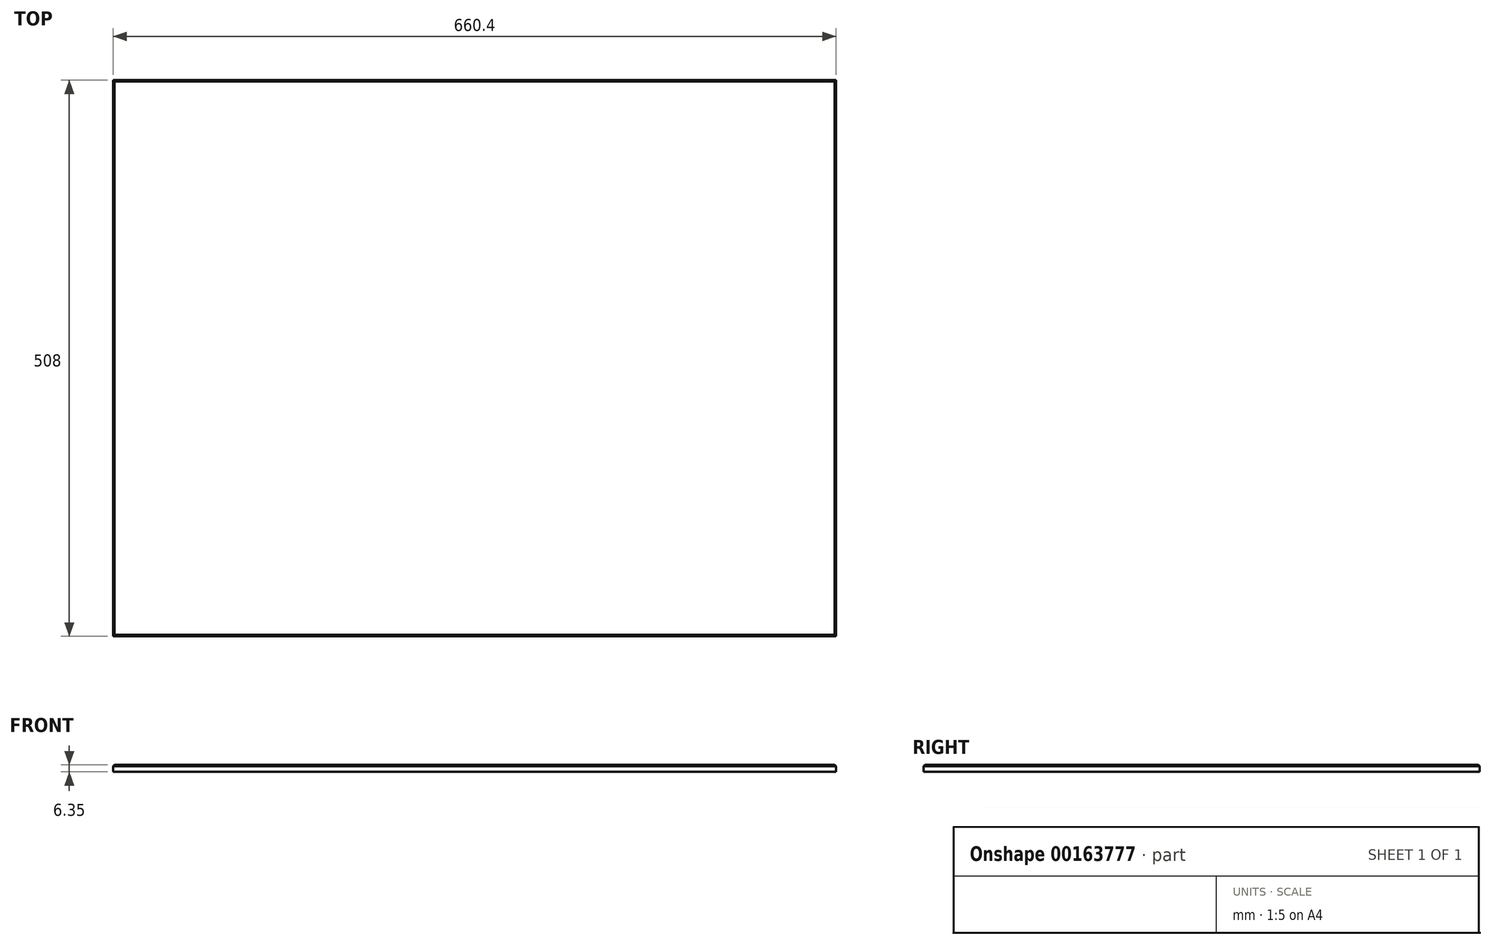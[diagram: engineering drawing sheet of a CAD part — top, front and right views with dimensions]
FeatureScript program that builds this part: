
annotation { "Feature Type Name" : "Feature", "Feature Type Description" : "" }
export const myFeature = defineFeature(function(context is Context, id is Id, definition is map)
    precondition{}
    {
        {
            var Q0;
            Q0=qCreatedBy(makeId("Top.planeOp"),FACE);
            var sketch = newSketch(context, id + "F0", { "sketchPlane" : qUnion([Q0])});
            skLineSegment(sketch, "E0.bottom", {"start": v(330.2, 254) * mm, "end": v(-330.2, 254) * mm});
            skLineSegment(sketch, "E0.top", {"start": v(330.2, -254) * mm, "end": v(-330.2, -254) * mm});
            skLineSegment(sketch, "E0.left", {"start": v(330.2, 254) * mm, "end": v(330.2, -254) * mm});
            skLineSegment(sketch, "E0.right", {"start": v(-330.2, 254) * mm, "end": v(-330.2, -254) * mm});
            skPoint(sketch, "E0.middle", {"position": v(0, 0) * mm});
            skSolve(sketch);
        }
        {
            var Q0;
            Q0=qSketchRegion(id+"F0",true);
            extrude(context, id + "F1", {"entities" : qUnion([Q0]), "depth" : 6.35 * mm});
        }
        {
            var Q0;
            Q0=makeQuery(id+"F1.opExtrude","CAP_FACE",FACE,{"disambiguationData":[OSD([sQuery(id+"F0.wireOp",EDGE,"E0.bottom"),sQuery(id+"F0.wireOp",EDGE,"E0.top"),sQuery(id+"F0.wireOp",EDGE,"E0.left"),sQuery(id+"F0.wireOp",EDGE,"E0.right")])],"isStart":false});
            chamfer(context, id + "F2", {"entities" : qUnion([Q0]), "width" : 1.27 * mm, "tangentPropagation" : true});
        }
    });
